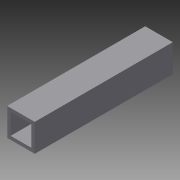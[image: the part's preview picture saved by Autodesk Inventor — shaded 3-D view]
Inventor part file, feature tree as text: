
AUTODESK INVENTOR PART (.ipt)
format: ipt  version: 2013 (Build 170138000, 138)  size: 72,192 bytes
history: native  units: in
note: dims shown in document units (in); Inventor stores cm internally (conversion verified against a paired STEP export)
features: extrude x1, sketch x1
ambient origin geometry x8: Origin, YZ Plane, XZ Plane, XY Plane, X Axis, Y Axis, Z Axis, Center Point
bodies: Solid1 (feature_tree)
feature tree (2):
  extrude  "Extrusion1"  Depth=1.0in
  sketch  "Sketch1"  dims[d0=1.0in d2=1.0in d3=0.125in d4=5.0in d5=0.0in]
